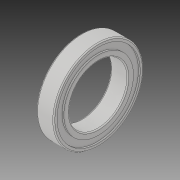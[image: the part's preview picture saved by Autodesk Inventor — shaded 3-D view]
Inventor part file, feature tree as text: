
AUTODESK INVENTOR PART (.ipt)
format: ipt  version: 2019 (Build 230136000, 136)  size: 151,040 bytes
history: native  units: in
note: dims shown in document units (in); Inventor stores cm internally (conversion verified against a paired STEP export)
features: fillet x1
ambient origin geometry x8: Origin, YZ Plane, XZ Plane, XY Plane, X Axis, Y Axis, Z Axis, Center Point
bodies: Solid1 (feature_tree)
feature tree (1):
  fillet  "Fillet1"  [1 undecoded]
note: 1 required parameter value undecoded (feature->parameter linkage not recoverable at this tier; creation-order binding heuristic only, values carry confidence <= 0.55)
